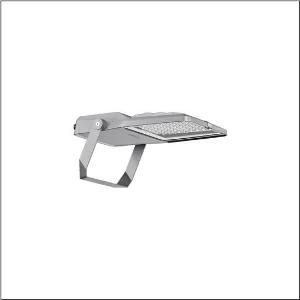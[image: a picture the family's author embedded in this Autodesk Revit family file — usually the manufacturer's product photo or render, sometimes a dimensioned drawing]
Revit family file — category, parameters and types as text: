
# Revit family: floodlight_fl_21_iq_mini___pl61_5xa7771b2c1a_d515
name_source: partatom
category: Lighting Fixtures
units: mm (PartAtom-declared; Revit-internal decimal feet)

## family parameters
Cut with Voids When Loaded = No
Host = Face
Light Source = No
Part Type = Normal
Room Calculation Point = No
Round Connector Dimension = Use Diameter
Shared = No

## types (1)
- --- (1 x LED, 6120 lm, 45.5 W, 3000K)
    Apparent Load = 46 VA
    CIE Flux Codes = 33 65 98 100 100
    Color Rendering = 70
    Color Temperature = 3000K
    Default Elevation = 1800 mm
    Description = Floodlight FL 21 iQ mini, floodlight, primary light control with lens, of PMMA, primary optical cover: protective disc, of toughened safety glass, transparent, light distribution: PL61, light emission: direct distribution, installation type: surface-mounted, lamps: LED, High Power LED, rated values: 6.120lm | 45,5W | 134,5lm/W (begin service life); end service life: 6.120lm | 48W; at 50% lumin. flux: 3.060lm | 21,5W | 142,3lm/W, colour temperature: 3000K, colour rendering: CRI > 70, light colour: 730, light setting 1 begin service life: 100% | 6.120lm | 45,5W | 134,5lm/W | 3.000K, light setting 1 end service life: 48W, further light settings possible, control: Auto-Match, Temp-Guard, Lumen-Switch, Night-Set, Smart-Wire, Light-Fading, Desk-Remote (wireless, voltage-free reading and setting of iQ features in the workshop via application-optimized NFC function/RFID function), optimised constant luminous flux control (CLO 2.0), pre-setting: linear dimming characteristic, with terminal, 6-pole, mains connection: 220..240V, AC, 50/60Hz, luminaire housing, of diecast aluminium, powder-coated, SITECO metallic grey (DB 702S), corrosivity category C5 mid according to DIN EN ISO 12944suitable for swimming poolschlorine-resistant, sealing non-destructively replaceable, mounting bracket, of steel, galvanised, powder-coated, SITECO metallic grey (DB 702S), protection rating (complete): IP66, insulation class (complete): insulation class II (safety insulation), certification: CE, ENEC, VDE, protection symbol: D, impact resistance: IK08, permissible operating ambient temperature: -40..+40°C, permissible operating ambient temperature for outdoor applications: -40..+50°C, standard: DIN EN 12944, LABS conformity tested according to VDMA 24364:2018-05, packaging unit: 1 piece

Light Distribution: PL61
    Height = 70 mm
    Lamp = 1 x LED
    Lamp Light Flux = 6120 lm
    Lamp Power = 45.5 W
    Lamp count = 1
    Length = 485 mm
    Luminous efficacy = 135 lm/W
    Manufacturer = Siteco
    ModVariant = No
    Model = 5XA7771B2C1A
    Mounting Place = Wall
    Mounting Type = Surface mounted
    Number of Poles = 1
    OnlyDefault = Yes
    Power Factor = 1
    Product Name = Floodlight FL 21 iQ mini | PL61
    Product group = floodlight | wall mounted
    ProductGroupID = 2002
    Protection Class = Protection class II
    Protection Degree = IP 66
    RLX_Detail_Level = 1
    RLX_Emergency_Light_Flux = 0 lm
    RLX_Emergency_Type = 0
    RLX_Emergency_Type_DB = No
    RlxData = <blob elided: 96373 chars, md5=e2e48eda>
    Socket = socket
    Standby Power = 0 W
    System Light Flux = 6120 lm
    System Power = 46 W
    Type Comments = factory setting: luminous flux: 100 % | dim-lin: 254 | 463 mA
    Type Image = l_1006845.jpg
    URL = http://relux.com
    VarID = @adj_174949
    Voltage = 0 V
    Weight = 0.00 kg
    Width = 337 mm

## geometry (parser evidence)
native form markers: Blend x4, Sweep x10
no freeform markers — native parametric forms only
